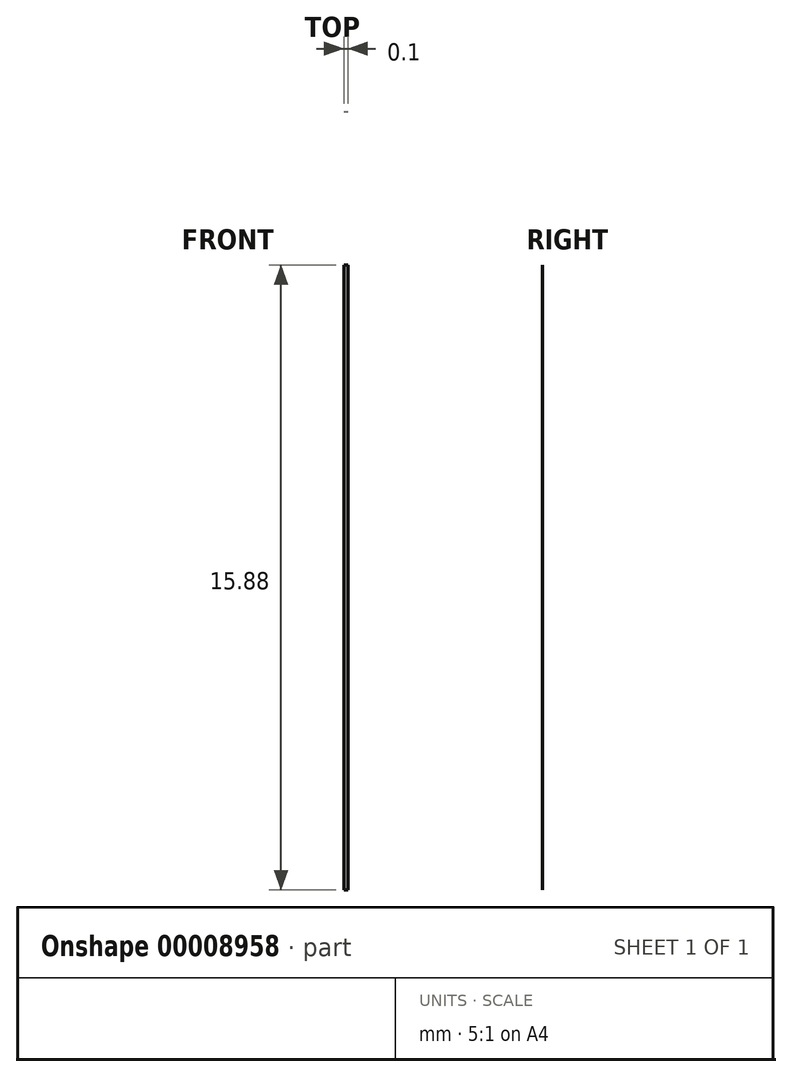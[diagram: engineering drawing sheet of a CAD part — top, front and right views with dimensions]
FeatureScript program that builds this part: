
annotation { "Feature Type Name" : "Feature", "Feature Type Description" : "" }
export const myFeature = defineFeature(function(context is Context, id is Id, definition is map)
    precondition{}
    {
        {
            var Q0;
            Q0=qCreatedBy(makeId("Top.planeOp"),FACE);
            var sketch = newSketch(context, id + "F0", { "sketchPlane" : qUnion([Q0])});
            skArc(sketch, "E0", {"start": v(6.24, 2.41) * mm, "mid": v(6.35, -2.41) * mm, "end": v(6.46, 2.41) * mm, "construction": true});
            skArc(sketch, "E1", {"start": v(12.9, -2.4) * mm, "mid": v(15.11, 0.04) * mm, "end": v(12.8, 2.41) * mm, "construction": true});
            skCircle(sketch, "E2", {"center": v(-6.35, 0) * mm, "radius": 3.43 * mm, "construction": true});
            skArc(sketch, "E3.0", {"start": v(-11.24, -3.43) * mm, "mid": v(-9.08, -5.3) * mm, "end": v(-6.3, -5.97) * mm});
            skArc(sketch, "E4.0", {"start": v(7.5, 2.41) * mm, "mid": v(3.68, 0) * mm, "end": v(7.49, -2.41) * mm});
            skArc(sketch, "E5.0", {"start": v(13.84, 2.41) * mm, "mid": v(12.7, 2.67) * mm, "end": v(11.56, 2.41) * mm});
            skLineSegment(sketch, "E6", {"start": v(7.49, -2.41) * mm, "end": v(11.56, -2.41) * mm});
            skLineSegment(sketch, "E7", {"start": v(12.7, -2.41) * mm, "end": v(12.9, -2.4) * mm});
            skArc(sketch, "E8", {"start": v(18.16, 2.41) * mm, "mid": v(15.96, 5) * mm, "end": v(12.7, 5.97) * mm});
            skLineSegment(sketch, "E9", {"start": v(-6.4, 5.97) * mm, "end": v(12.7, 5.97) * mm});
            skLineSegment(sketch, "E10", {"start": v(-6.4, -5.97) * mm, "end": v(12.7, -5.97) * mm});
            skLineSegment(sketch, "E11", {"start": v(6.24, 2.41) * mm, "end": v(6.46, 2.41) * mm});
            skArc(sketch, "E12.0", {"start": v(-7.7, -3.43) * mm, "mid": v(-2.67, 0.04) * mm, "end": v(-7.76, 3.4) * mm});
            skLineSegment(sketch, "E13", {"start": v(-6.42, 3.43) * mm, "end": v(-11.3, 3.33) * mm});
            skLineSegment(sketch, "E14", {"start": v(-6.34, -3.43) * mm, "end": v(-11.24, -3.43) * mm});
            skArc(sketch, "E15.trimOffspring", {"start": v(11.56, -2.41) * mm, "mid": v(12.76, -2.67) * mm, "end": v(13.94, -2.36) * mm});
            skLineSegment(sketch, "E16.trimOffspring", {"start": v(13.84, 2.41) * mm, "end": v(18.16, 2.41) * mm});
            skLineSegment(sketch, "E17.trimOffspring", {"start": v(13.94, -2.36) * mm, "end": v(18.25, -2.19) * mm});
            skArc(sketch, "E18.trimOffspring", {"start": v(12.7, -5.97) * mm, "mid": v(16.06, -4.93) * mm, "end": v(18.25, -2.19) * mm});
            skLineSegment(sketch, "E19.trimOffspring", {"start": v(7.5, 2.41) * mm, "end": v(11.56, 2.41) * mm});
            skArc(sketch, "E20.trimOffspring", {"start": v(12.6, 2.41) * mm, "mid": v(10.29, -0.05) * mm, "end": v(12.7, -2.41) * mm, "construction": true});
            skArc(sketch, "E21.trimOffspring", {"start": v(-6.3, 5.97) * mm, "mid": v(-9.13, 5.28) * mm, "end": v(-11.3, 3.33) * mm});
            skSolve(sketch);
        }
        {
            var Q0;
            {var subQ1=sQuery(id+"F0.wireOp",EDGE,"E3.0");Q0=makeQuery(id+"F0.imprint","IMPRINT",FACE,{"disambiguationData":[TD([[makeQuery(id+"F0.imprint","IMPRINT",EDGE,{"derivedFrom":subQ1}),1.0]])]});}
            extrude(context, id + "F1", {"entities" : qUnion([Q0]), "depth" : 15.88 * mm, "offsetDistance" : 25.4 * mm});
        }
    });
